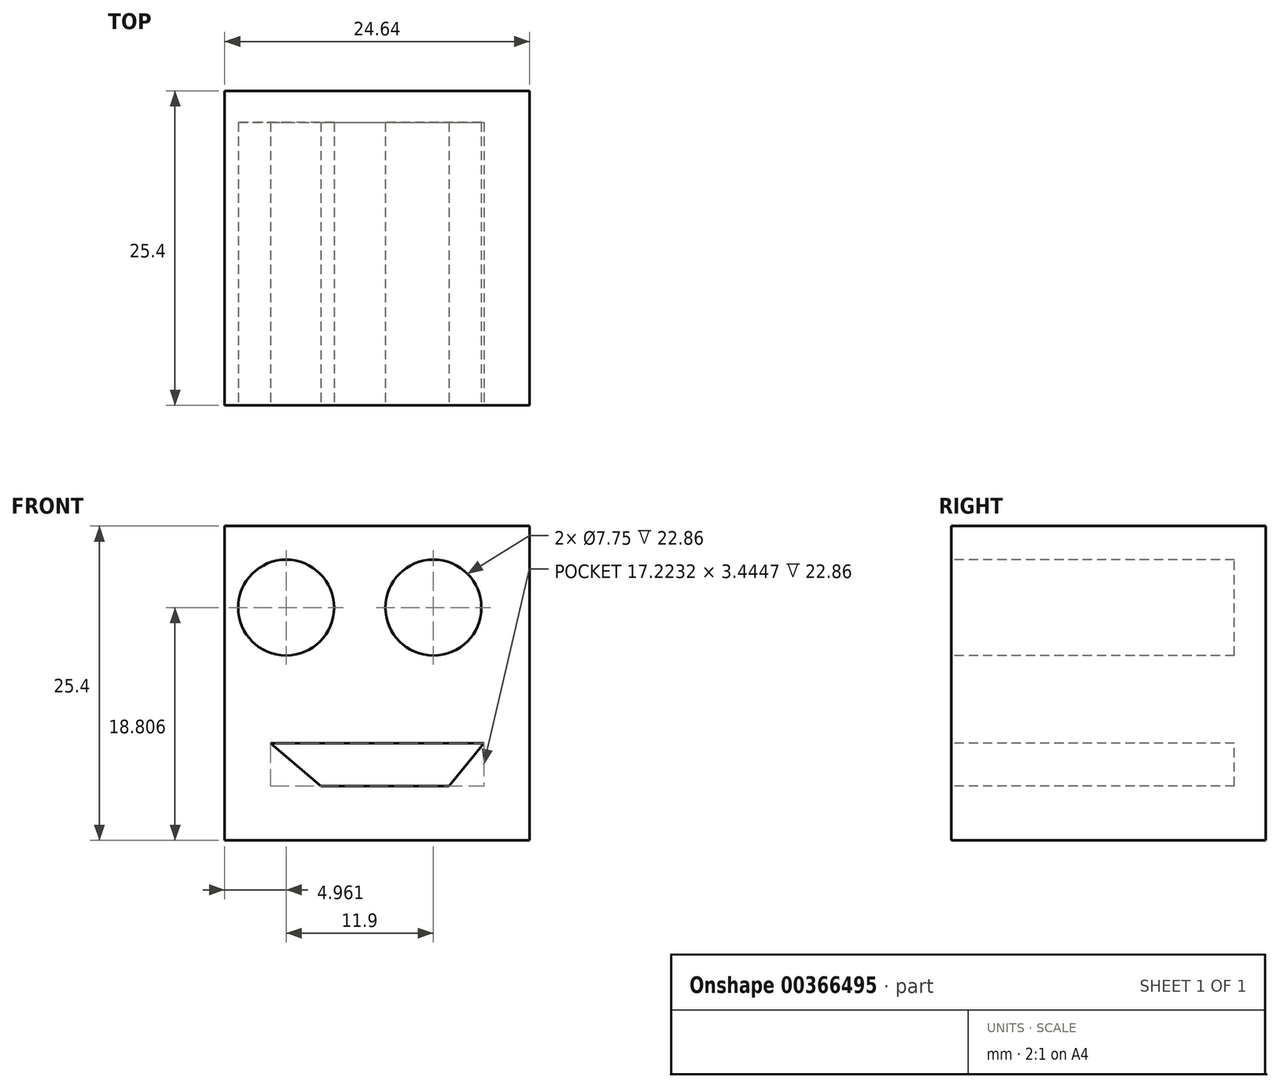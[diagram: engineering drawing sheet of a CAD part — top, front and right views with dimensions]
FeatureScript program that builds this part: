
annotation { "Feature Type Name" : "Feature", "Feature Type Description" : "" }
export const myFeature = defineFeature(function(context is Context, id is Id, definition is map)
    precondition{}
    {
        {
            var Q0;
            Q0=qCreatedBy(makeId("Front.planeOp"),FACE);
            var sketch = newSketch(context, id + "F0", { "sketchPlane" : qUnion([Q0])});
            skPoint(sketch, "E0.middle", {"position": v(0, 0) * mm});
            skLineSegment(sketch, "E1.bottom", {"start": v(12.32, -12.7) * mm, "end": v(-12.32, -12.7) * mm});
            skLineSegment(sketch, "E1.top", {"start": v(12.32, 12.7) * mm, "end": v(-12.32, 12.7) * mm});
            skLineSegment(sketch, "E1.left", {"start": v(12.32, -12.7) * mm, "end": v(12.32, 12.7) * mm});
            skLineSegment(sketch, "E1.right", {"start": v(-12.32, -12.7) * mm, "end": v(-12.32, 12.7) * mm});
            skSolve(sketch);
        }
        {
            var Q0;
            Q0=makeQuery(id+"F0.imprint","IMPRINT",FACE,{"disambiguationData":[TD([[makeQuery(id+"F0.imprint","IMPRINT",EDGE,{"derivedFrom":sQuery(id+"F0.wireOp",EDGE,"E1.bottom")}),-1.0]])]});
            extrude(context, id + "F1", {"entities" : qUnion([Q0]), "depth" : 25.4 * mm});
        }
        {
            var Q0;
            Q0=makeQuery(id+"F1.opExtrude","CAP_FACE",FACE,{"disambiguationData":[OSD([sQuery(id+"F0.wireOp",EDGE,"E1.bottom"),sQuery(id+"F0.wireOp",EDGE,"E1.top"),sQuery(id+"F0.wireOp",EDGE,"E1.left"),sQuery(id+"F0.wireOp",EDGE,"E1.right")])],"isStart":false});
            var sketch = newSketch(context, id + "F2", { "sketchPlane" : qUnion([Q0])});
            skCircle(sketch, "E2", {"center": v(-7.36, 6.1) * mm, "radius": 3.87 * mm});
            skCircle(sketch, "E3", {"center": v(4.54, 6.1) * mm, "radius": 3.87 * mm});
            skLineSegment(sketch, "E4", {"start": v(-8.61, -4.85) * mm, "end": v(-4.54, -8.3) * mm});
            skLineSegment(sketch, "E5", {"start": v(-4.54, -8.3) * mm, "end": v(0, -8.3) * mm});
            skLineSegment(sketch, "E6", {"start": v(0, -8.3) * mm, "end": v(5.8, -8.3) * mm});
            skLineSegment(sketch, "E7", {"start": v(5.8, -8.3) * mm, "end": v(8.61, -4.85) * mm});
            skLineSegment(sketch, "E8", {"start": v(-8.61, -4.85) * mm, "end": v(8.61, -4.85) * mm});
            skLineSegment(sketch, "E9", {"start": v(8.36, -4.88) * mm, "end": v(8.61, -4.85) * mm});
            skSolve(sketch);
        }
        {
            var Q0;
            Q0=makeQuery(id+"F2.imprint","IMPRINT",FACE,{"disambiguationData":[TD([[makeQuery(id+"F2.imprint","IMPRINT",EDGE,{"derivedFrom":sQuery(id+"F2.wireOp",EDGE,"E4")}),1.0]])]});
            var Q1;
            Q1=makeQuery(id+"F2.imprint","IMPRINT",FACE,{"disambiguationData":[TD([[makeQuery(id+"F2.imprint","IMPRINT",EDGE,{"derivedFrom":sQuery(id+"F2.wireOp",EDGE,"E3")}),1.0]])]});
            var Q2;
            Q2=makeQuery(id+"F2.imprint","IMPRINT",FACE,{"disambiguationData":[TD([[makeQuery(id+"F2.imprint","IMPRINT",EDGE,{"derivedFrom":sQuery(id+"F2.wireOp",EDGE,"E2")}),1.0]])]});
            extrude(context, id + "F3", {"entities" : qUnion([Q0, Q1, Q2]), "operationType" : NewBodyOperationType.REMOVE, "oppositeDirection" : true, "depth" : 22.86 * mm});
        }
    });
